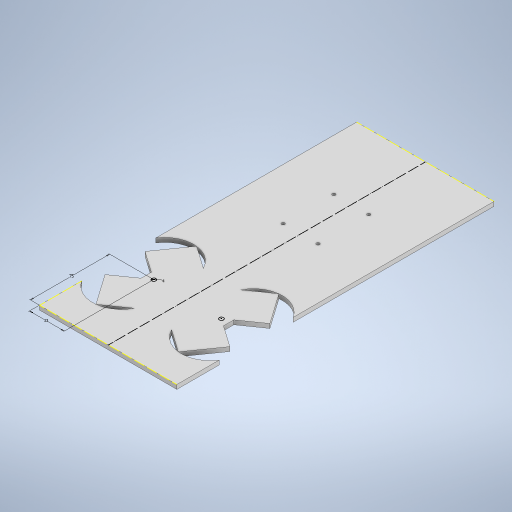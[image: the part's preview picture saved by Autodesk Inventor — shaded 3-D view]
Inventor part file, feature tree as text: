
AUTODESK INVENTOR PART (.ipt)
format: ipt  version: 2023.2 (Build 272271000, 271)  size: 339,456 bytes
history: native  units: mm
features: sketch x3, hole x1
ambient origin geometry x8: Origin, YZ Plane, XZ Plane, XY Plane, X Axis, Y Axis, Z Axis, Center Point
bodies: Body1 (feature_tree)
feature tree (4):
  hole  "Hole1"  [1 undecoded]
  sketch  "Sketch13"  dims[d158=33.0mm d159=6.108652mm d160=6.108652mm d161=4.0mm d169=6.108652mm d170=6.108652mm d172=75.0mm d175=33.0mm d179=33.0mm d181=4.0mm d182=0.0mm d183=70.0mm d185=26.0mm d186=35.0mm d187=26.0mm d188=75.0mm d189=70.0mm d190=26.0mm d191=75.0mm d196=3.0mm d201=33.0mm d202=48.0mm d205=75.0mm d208=3.0mm d209=5.0mm d210=3.0mm d211=6.0mm d212=4.0mm d213=2.0mm d214=90.0deg d215=8.0mm d216=20.594885mm d217=75.0mm d219=4.0mm d220=33.0mm d9=0.5mm d10=0.872665mm d11=0.5mm d12=0.872665mm d13=0.5mm d14=0.872665mm d27=0.5mm d28=0.872665mm d29=0.5mm d30=0.872665mm d88=0.5mm d89=0.872665mm d90=0.5mm d91=0.872665mm d116=0.5mm d117=0.872665mm d118=0.5mm d119=0.872665mm d154=0.5mm d155=0.872665mm d156=0.5mm d157=0.872665mm d184=0.872665mm]
  sketch  "Sketch1"  dims[d122=130.0mm d123=300.0mm]
  sketch  "Sketch12"  dims[d128=75.0mm]
note: 1 required parameter value undecoded (feature->parameter linkage not recoverable at this tier; creation-order binding heuristic only, values carry confidence <= 0.55)
